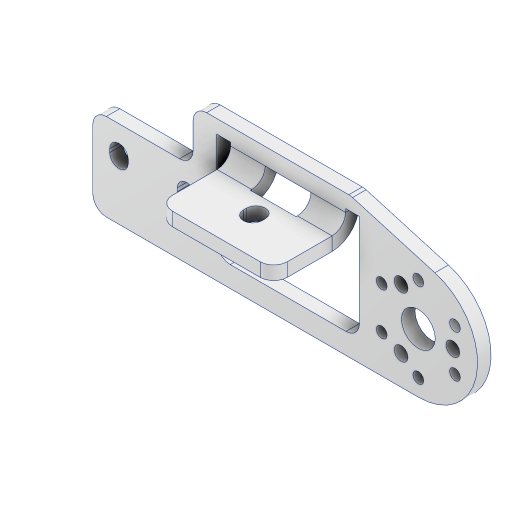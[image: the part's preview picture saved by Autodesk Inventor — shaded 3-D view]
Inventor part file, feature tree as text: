
AUTODESK INVENTOR PART (.ipt)
format: ipt  version: 2023 (Build 270158000, 158)  size: 276,992 bytes
history: native  units: mm
features: other x3, sketch x3, fillet x1, hole x1
ambient origin geometry x8: Origin, YZ Plane, XZ Plane, XY Plane, X Axis, Y Axis, Z Axis, Center Point
bodies: Body1 (feature_tree)
feature tree (8):
  other  "ソリッド1"
  other  "折り曲げ4"
  fillet  "フィレット1"  Radius=35.0mm
  hole  "穴1"  [1 undecoded]
  sketch  "スケッチ1"
  other  "プレート1"
  sketch  "スケッチ5"
  sketch  "スケッチ6"
note: 1 required parameter value undecoded (feature->parameter linkage not recoverable at this tier; creation-order binding heuristic only, values carry confidence <= 0.55)
